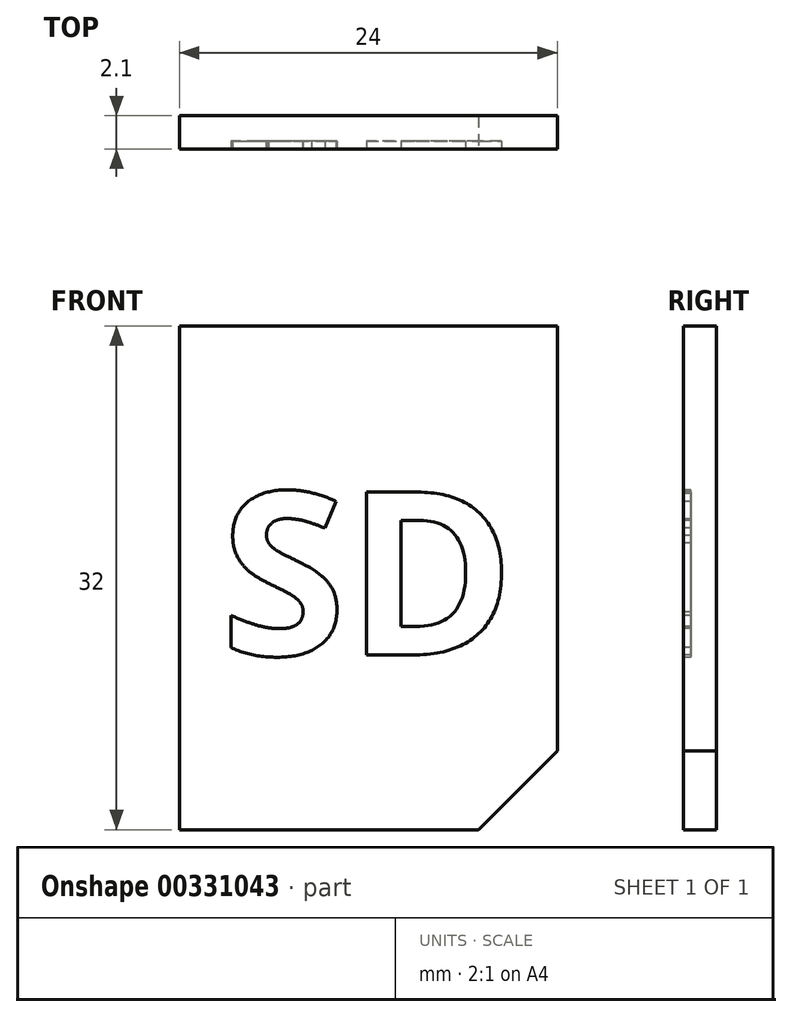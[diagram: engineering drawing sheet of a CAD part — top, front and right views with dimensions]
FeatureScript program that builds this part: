
annotation { "Feature Type Name" : "Feature", "Feature Type Description" : "" }
export const myFeature = defineFeature(function(context is Context, id is Id, definition is map)
    precondition{}
    {
        {
            var Q0;
            Q0=qCreatedBy(makeId("Front.planeOp"),FACE);
            var sketch = newSketch(context, id + "F0", { "sketchPlane" : qUnion([Q0])});
            skLineSegment(sketch, "E0.bottom", {"start": v(12, -16) * mm, "end": v(-12, -16) * mm});
            skLineSegment(sketch, "E0.top", {"start": v(12, 16) * mm, "end": v(-12, 16) * mm});
            skLineSegment(sketch, "E0.left", {"start": v(12, -16) * mm, "end": v(12, 16) * mm});
            skLineSegment(sketch, "E0.right", {"start": v(-12, -16) * mm, "end": v(-12, 16) * mm});
            skPoint(sketch, "E0.middle", {"position": v(0, 0) * mm});
            skSolve(sketch);
        }
        {
            var Q0;
            Q0=makeQuery(id+"F0.imprint","IMPRINT",FACE,{"disambiguationData":[TD([[makeQuery(id+"F0.imprint","IMPRINT",EDGE,{"derivedFrom":sQuery(id+"F0.wireOp",EDGE,"E0.bottom")}),-1.0]])]});
            extrude(context, id + "F1", {"entities" : qUnion([Q0]), "depth" : 2.1 * mm});
        }
        {
            var Q0;
            Q0=makeQuery(id+"F1.opExtrude","SWEPT_EDGE",EDGE,{"disambiguationData":[OSD([sQuery(id+"F0.wireOp",EDGE,"E0.bottom"),sQuery(id+"F0.wireOp",EDGE,"E0.left")])]});
            chamfer(context, id + "F2", {"entities" : qUnion([Q0]), "width" : 5 * mm, "tangentPropagation" : true});
        }
        {
            var Q0;
            Q0=makeQuery(id+"F1.opExtrude","CAP_FACE",FACE,{"disambiguationData":[OSD([sQuery(id+"F0.wireOp",EDGE,"E0.bottom"),sQuery(id+"F0.wireOp",EDGE,"E0.top"),sQuery(id+"F0.wireOp",EDGE,"E0.left"),sQuery(id+"F0.wireOp",EDGE,"E0.right")])],"isStart":false});
            var sketch = newSketch(context, id + "F3", { "sketchPlane" : qUnion([Q0])});
            skText(sketch, "E1", { "text": "SD", "fontName": "OpenSans-Bold.ttf"});
            skPoint(sketch, "E2", {"position": v(0, 0) * mm});
            const initialGuessF3  = {"E1": [-0.0094, -0.0049, 1, 0, 0.01043]};
            skSetInitialGuess(sketch, initialGuessF3);
            skSolve(sketch);
        }
        {
            var Q0;
            Q0 = qSketchRegion(id + "F3", true);
            extrude(context, id + "F4", {"entities" : qUnion([Q0]), "operationType" : NewBodyOperationType.REMOVE, "oppositeDirection" : true, "depth" : 0.5 * mm});
        }
    });
